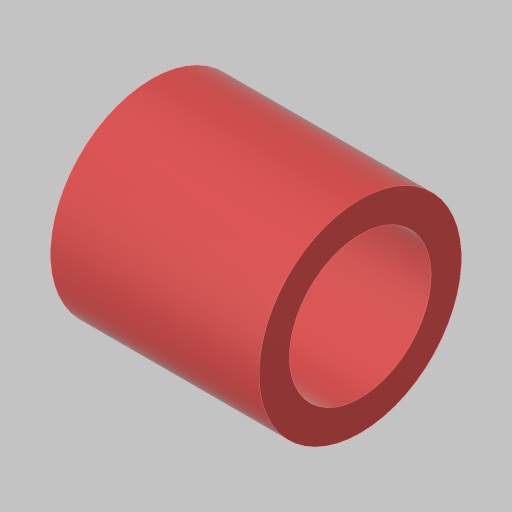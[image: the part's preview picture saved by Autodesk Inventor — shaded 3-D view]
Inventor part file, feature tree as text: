
AUTODESK INVENTOR PART (.ipt)
format: ipt  version: 2023.5 (Build 275446000, 446)  size: 114,688 bytes
history: native  units: in
note: dims shown in document units (in); Inventor stores cm internally (conversion verified against a paired STEP export)
features: extrude x1, sketch x1
ambient origin geometry x8: Origin, YZ Plane, XZ Plane, XY Plane, X Axis, Y Axis, Z Axis, Center Point
bodies: Solid1 (feature_tree)
feature tree (2):
  extrude  "Extrusion1"  Depth=0.86in
  sketch  "Sketch1"  dims[d0=0.585in d1=0.125in d2=0.86in d3=0.0in]
